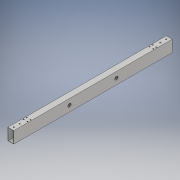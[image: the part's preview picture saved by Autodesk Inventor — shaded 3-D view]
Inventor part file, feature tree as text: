
AUTODESK INVENTOR PART (.ipt)
format: ipt  version: 2018 (Build 220112000, 112)  size: 166,400 bytes
history: native  units: in
note: dims shown in document units (in); Inventor stores cm internally (conversion verified against a paired STEP export)
features: extrude x4, sketch x4
ambient origin geometry x8: Origin, YZ Plane, XZ Plane, XY Plane, X Axis, Y Axis, Z Axis, Center Point
bodies: Solid1 (feature_tree)
feature tree (8):
  extrude  "Extrusion1"  Depth=2.0in
  extrude  "Extrusion2"  Depth=27.0in TaperAngle=0.0deg
  extrude  "Extrusion9"  Depth=1.0in
  extrude  "Extrusion10"  Depth=1.0in TaperAngle=0.0deg
  sketch  "Sketch1"  dims[d0=1.0in d1=2.0in]
  sketch  "Sketch2"  dims[d2=0.0625in d3=27.0in d4=0.0in]
  sketch  "Sketch6"  dims[d5=0.5in d6=1.0in]
  sketch  "Sketch7"  dims[d7=0.2031in d8=6.5in d9=0.0in d32=9.5in d33=0.59in d34=1.0in d35=0.0in d37=3.2815in d38=0.25in d39=0.187in d40=0.6299in d41=0.5315in d42=0.1811in d43=3.9375in d44=0.0in d45=0.1811in d46=0.1811in d47=0.1811in]
